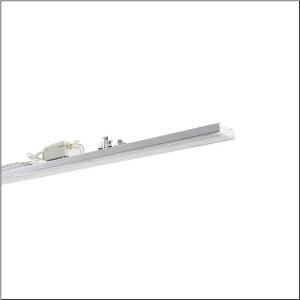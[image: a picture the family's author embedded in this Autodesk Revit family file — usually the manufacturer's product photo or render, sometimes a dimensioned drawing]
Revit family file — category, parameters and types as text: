
# Revit family: licross_r__21_recessed_ho_52tl12dv4l2m_1f59
name_source: partatom
category: Lighting Fixtures
units: mm (PartAtom-declared; Revit-internal decimal feet)

## family parameters
Cut with Voids When Loaded = No
Host = Face
Light Source = No
Part Type = Normal
Room Calculation Point = No
Round Connector Dimension = Use Diameter
Shared = No

## types (1)
- --- (1 x LED, 22710 lm, 125.6 W, 4000K)
    Apparent Load = 126 VA
    CIE Flux Codes = 69 91 98 100 100
    Color Rendering = 80
    Color Temperature = 4000K
    Default Elevation = 1800 mm
    Description = Licross® 21 Recessed HO, luminaire insert, of sheet steel, galvanised, coil coated, white, length: 2.250mm, width: 66mm, height: 67mm, LED rated luminous flux: 22.710lm, light colour: 840, control gear: DALI 2, with plug, 5-pole, with phase selection, mains connection: 220..240V, AC, 50/60Hz, rated input power: 126W, halogen-free wiring, primary optical cover: cover, of PMMA, light emission: direct distribution, primary light characteristic: symmetric, protection rating (complete): IP40, insulation class (complete): insulation class I (protective earthing), certification: CE, ENEC, VDE, UKCA, protection symbol: D if used in an environment without relevant dust loads with corresponding accessories, impact resistance: IK06, permissible ambient temperature for indoor applications: -40..+30°C, corresponds to IFS (International Featured Standards) requirements for safety and quality in the food industry, reducing of maximum allowable ambient temperature of 5°C with ceiling mounting, LABS conformity tested according to VDMA 24364:2018-05, packaging unit: 1 piece
    Height = 58 mm
    Lamp = 1 x LED
    Lamp Light Flux = 22710 lm
    Lamp Power = 125.6 W
    Lamp count = 1
    Length = 2250 mm
    Luminous efficacy = 181 lm/W
    Manufacturer = Siteco
    ModVariant = No
    Model = 52TL12DV4L2M
    Mounting Place = Ceiling
    Mounting Type = Pendant
    Number of Poles = 1
    OnlyDefault = Yes
    Power Factor = 1
    Product Name = Licross® 21 Recessed HO
    Product group = luminaire insert
    ProductGroupID = 901
    Protection Class = Protection class I
    Protection Degree = IP 40
    RLX_Detail_Level = 1
    RLX_Emergency_Light_Flux = 0 lm
    RLX_Emergency_Type = 0
    RLX_Emergency_Type_DB = No
    RlxData = <blob elided: 29557 chars, md5=d474d39c>
    Socket = socket
    Standby Power = 0 W
    System Light Flux = 22710 lm
    System Power = 126 W
    Type Comments = factory setting: luminous flux: 100 % | dim-lin: 254 | 489 mA
    Type Image = l_1296930.jpg
    URL = http://relux.com
    VarID = @adj_046765
    Voltage = 0 V
    Weight = 0.00 kg
    Width = 66 mm

## geometry (parser evidence)
native form markers: Blend x4, Sweep x10
no freeform markers — native parametric forms only
